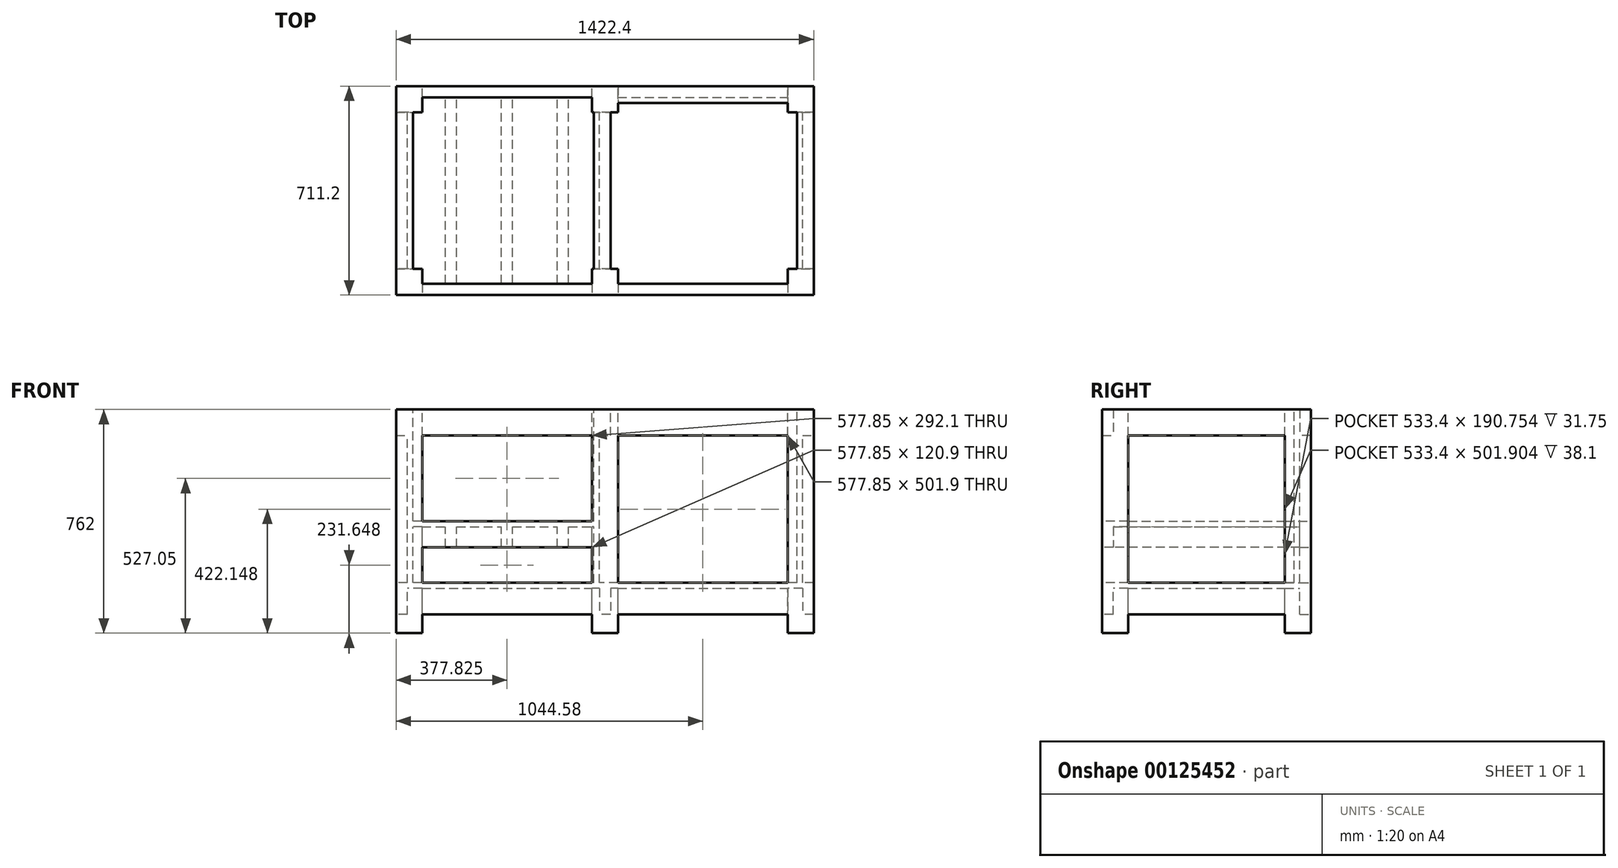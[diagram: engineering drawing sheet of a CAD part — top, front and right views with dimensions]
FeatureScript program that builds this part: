
annotation { "Feature Type Name" : "Feature", "Feature Type Description" : "" }
export const myFeature = defineFeature(function(context is Context, id is Id, definition is map)
    precondition{}
    {
        {
            var Q0;
            Q0=qCreatedBy(makeId("Top.planeOp"),FACE);
            var sketch = newSketch(context, id + "F0", { "sketchPlane" : qUnion([Q0])});
            skLineSegment(sketch, "E0", {"start": v(-711.2, 0) * mm, "end": v(711.2, 0) * mm});
            skLineSegment(sketch, "E1", {"start": v(711.2, 0) * mm, "end": v(711.2, -711.2) * mm});
            skLineSegment(sketch, "E2", {"start": v(711.2, -711.2) * mm, "end": v(-711.2, -711.2) * mm});
            skLineSegment(sketch, "E3", {"start": v(-711.2, -711.2) * mm, "end": v(-711.2, 0) * mm});
            skLineSegment(sketch, "E4.0", {"start": v(673.1, -673.1) * mm, "end": v(19.05, -673.1) * mm});
            skLineSegment(sketch, "E4.1", {"start": v(673.1, -38.1) * mm, "end": v(673.1, -673.1) * mm});
            skLineSegment(sketch, "E4.2", {"start": v(-673.1, -38.1) * mm, "end": v(-19.05, -38.1) * mm});
            skLineSegment(sketch, "E4.3", {"start": v(-673.1, -673.1) * mm, "end": v(-673.1, -38.1) * mm});
            skLineSegment(sketch, "E5", {"start": v(0, 0) * mm, "end": v(0, -711.2) * mm, "construction": true});
            skLineSegment(sketch, "E6.0", {"start": v(-19.05, -38.1) * mm, "end": v(-19.05, -673.1) * mm});
            skLineSegment(sketch, "E7.0", {"start": v(19.05, -38.1) * mm, "end": v(19.05, -673.1) * mm});
            skLineSegment(sketch, "E8.trimOffspring", {"start": v(-19.05, -673.1) * mm, "end": v(-673.1, -673.1) * mm});
            skLineSegment(sketch, "E9.trimOffspring", {"start": v(19.05, -38.1) * mm, "end": v(673.1, -38.1) * mm});
            skSolve(sketch);
        }
        {
            var Q0;
            Q0=makeQuery(id+"F0.imprint","IMPRINT",FACE,{"disambiguationData":[TD([[makeQuery(id+"F0.imprint","IMPRINT",EDGE,{"derivedFrom":sQuery(id+"F0.wireOp",EDGE,"E0")}),-1.0]])]});
            extrude(context, id + "F1", {"entities" : qUnion([Q0]), "oppositeDirection" : true, "depth" : 88.9 * mm});
        }
        {
            var Q0;
            Q0=qCreatedBy(makeId("Top.planeOp"),FACE);
            var sketch = newSketch(context, id + "F2", { "sketchPlane" : qUnion([Q0])});
            skLineSegment(sketch, "E10.bottom", {"start": v(-711.2, 0) * mm, "end": v(-622.3, 0) * mm});
            skLineSegment(sketch, "E10.top", {"start": v(-711.2, -88.9) * mm, "end": v(-622.3, -88.9) * mm});
            skLineSegment(sketch, "E10.left", {"start": v(-711.2, 0) * mm, "end": v(-711.2, -88.9) * mm});
            skLineSegment(sketch, "E10.right", {"start": v(-622.3, 0) * mm, "end": v(-622.3, -88.9) * mm});
            skLineSegment(sketch, "E11.bottom", {"start": v(-711.2, -711.2) * mm, "end": v(-622.3, -711.2) * mm});
            skLineSegment(sketch, "E11.top", {"start": v(-711.2, -622.3) * mm, "end": v(-622.3, -622.3) * mm});
            skLineSegment(sketch, "E11.left", {"start": v(-711.2, -711.2) * mm, "end": v(-711.2, -622.3) * mm});
            skLineSegment(sketch, "E11.right", {"start": v(-622.3, -711.2) * mm, "end": v(-622.3, -622.3) * mm});
            skLineSegment(sketch, "E12.bottom", {"start": v(-44.45, 0) * mm, "end": v(44.45, 0) * mm});
            skLineSegment(sketch, "E12.top", {"start": v(-44.45, -88.9) * mm, "end": v(44.45, -88.9) * mm});
            skLineSegment(sketch, "E12.left", {"start": v(-44.45, 0) * mm, "end": v(-44.45, -88.9) * mm});
            skLineSegment(sketch, "E12.right", {"start": v(44.45, 0) * mm, "end": v(44.45, -88.9) * mm});
            skLineSegment(sketch, "E13.bottom", {"start": v(-44.45, -711.2) * mm, "end": v(44.45, -711.2) * mm});
            skLineSegment(sketch, "E13.top", {"start": v(-44.45, -622.3) * mm, "end": v(44.45, -622.3) * mm});
            skLineSegment(sketch, "E13.left", {"start": v(-44.45, -711.2) * mm, "end": v(-44.45, -622.3) * mm});
            skLineSegment(sketch, "E13.right", {"start": v(44.45, -711.2) * mm, "end": v(44.45, -622.3) * mm});
            skLineSegment(sketch, "E14.bottom", {"start": v(622.3, -88.9) * mm, "end": v(711.2, -88.9) * mm});
            skLineSegment(sketch, "E14.top", {"start": v(622.3, 0) * mm, "end": v(711.2, 0) * mm});
            skLineSegment(sketch, "E14.left", {"start": v(622.3, -88.9) * mm, "end": v(622.3, 0) * mm});
            skLineSegment(sketch, "E14.right", {"start": v(711.2, -88.9) * mm, "end": v(711.2, 0) * mm});
            skLineSegment(sketch, "E15.bottom", {"start": v(622.3, -711.2) * mm, "end": v(711.2, -711.2) * mm});
            skLineSegment(sketch, "E15.top", {"start": v(622.3, -622.3) * mm, "end": v(711.2, -622.3) * mm});
            skLineSegment(sketch, "E15.left", {"start": v(622.3, -711.2) * mm, "end": v(622.3, -622.3) * mm});
            skLineSegment(sketch, "E15.right", {"start": v(711.2, -711.2) * mm, "end": v(711.2, -622.3) * mm});
            skSolve(sketch);
        }
        {
            var Q0;
            Q0 = qSketchRegion(id + "F2", true);
            extrude(context, id + "F3", {"entities" : qUnion([Q0]), "operationType" : NewBodyOperationType.ADD, "oppositeDirection" : true, "depth" : 762 * mm});
        }
        {
            var Q0;
            Q0=qCreatedBy(makeId("Top.planeOp"),FACE);
            cPlane(context, id + "F4", {"entities" : qUnion([Q0]), "cplaneType" : CPlaneType.OFFSET, "offset" : 609.6 * mm, "oppositeDirection" : true, "width" : 152.4 * mm, "height" : 152.4 * mm});
        }
        {
            var Q0;
            Q0=qCreatedBy(id+"F4.planeOp",FACE);
            var sketch = newSketch(context, id + "F5", { "sketchPlane" : qUnion([Q0])});
            skLineSegment(sketch, "E16", {"start": v(-711.2, 0) * mm, "end": v(711.2, 0) * mm});
            skLineSegment(sketch, "E17", {"start": v(711.2, 0) * mm, "end": v(711.2, -711.2) * mm});
            skLineSegment(sketch, "E18", {"start": v(711.2, -711.2) * mm, "end": v(-711.2, -711.2) * mm});
            skLineSegment(sketch, "E19", {"start": v(-711.2, -711.2) * mm, "end": v(-711.2, 0) * mm});
            skLineSegment(sketch, "E20.0", {"start": v(673.1, -673.1) * mm, "end": v(19.05, -673.1) * mm});
            skLineSegment(sketch, "E20.1", {"start": v(673.1, -38.1) * mm, "end": v(673.1, -673.1) * mm});
            skLineSegment(sketch, "E20.2", {"start": v(-673.1, -38.1) * mm, "end": v(-19.05, -38.1) * mm});
            skLineSegment(sketch, "E20.3", {"start": v(-673.1, -673.1) * mm, "end": v(-673.1, -38.1) * mm});
            skLineSegment(sketch, "E21", {"start": v(0, 1297.1) * mm, "end": v(0, -711.2) * mm, "construction": true});
            skLineSegment(sketch, "E22.0", {"start": v(-19.05, -38.1) * mm, "end": v(-19.05, -673.1) * mm});
            skLineSegment(sketch, "E23.0", {"start": v(19.05, -38.1) * mm, "end": v(19.05, -673.1) * mm});
            skLineSegment(sketch, "E24.trimOffspring", {"start": v(-19.05, -673.1) * mm, "end": v(-673.1, -673.1) * mm});
            skLineSegment(sketch, "E25.trimOffspring", {"start": v(19.05, -38.1) * mm, "end": v(673.1, -38.1) * mm});
            skSolve(sketch);
        }
        {
            var Q0;
            Q0 = qSketchRegion(id + "F5", true);
            extrude(context, id + "F6", {"entities" : qUnion([Q0]), "operationType" : NewBodyOperationType.ADD, "oppositeDirection" : true, "depth" : 88.9 * mm});
        }
        {
            var Q0;
            Q0=qCreatedBy(id+"F4.planeOp",FACE);
            var sketch = newSketch(context, id + "F7", { "sketchPlane" : qUnion([Q0])});
            skLineSegment(sketch, "E26.bottom", {"start": v(-711.2, 0) * mm, "end": v(711.2, 0) * mm});
            skLineSegment(sketch, "E26.top", {"start": v(-711.2, -711.2) * mm, "end": v(711.2, -711.2) * mm});
            skLineSegment(sketch, "E26.left", {"start": v(-711.2, 0) * mm, "end": v(-711.2, -711.2) * mm});
            skLineSegment(sketch, "E26.right", {"start": v(711.2, 0) * mm, "end": v(711.2, -711.2) * mm});
            skSolve(sketch);
        }
        {
            var Q0;
            Q0 = qSketchRegion(id + "F7", true);
            extrude(context, id + "F8", {"entities" : qUnion([Q0]), "operationType" : NewBodyOperationType.ADD, "depth" : 18.8 * mm, "hasSecondDirection" : true, "secondDirectionOppositeDirection" : true, "secondDirectionDepth" : 0.25 * mm});
        }
        {
            var Q0;
            Q0=qCreatedBy(makeId("Top.planeOp"),FACE);
            var sketch = newSketch(context, id + "F9", { "sketchPlane" : qUnion([Q0])});
            skLineSegment(sketch, "E27.bottom", {"start": v(673.1, -88.9) * mm, "end": v(654.05, -88.9) * mm});
            skLineSegment(sketch, "E27.top", {"start": v(673.1, -622.3) * mm, "end": v(654.05, -622.3) * mm});
            skLineSegment(sketch, "E27.left", {"start": v(673.1, -88.9) * mm, "end": v(673.1, -622.3) * mm});
            skLineSegment(sketch, "E27.right", {"start": v(654.05, -88.9) * mm, "end": v(654.05, -622.3) * mm});
            skLineSegment(sketch, "E28.bottom", {"start": v(622.3, -57.15) * mm, "end": v(44.45, -57.15) * mm});
            skLineSegment(sketch, "E28.top", {"start": v(622.3, -38.1) * mm, "end": v(44.45, -38.1) * mm});
            skLineSegment(sketch, "E28.left", {"start": v(622.3, -57.15) * mm, "end": v(622.3, -38.1) * mm});
            skLineSegment(sketch, "E28.right", {"start": v(44.45, -57.15) * mm, "end": v(44.45, -38.1) * mm});
            skLineSegment(sketch, "E29.bottom", {"start": v(-19.05, -88.9) * mm, "end": v(-38.1, -88.9) * mm});
            skLineSegment(sketch, "E29.top", {"start": v(-19.05, -622.3) * mm, "end": v(-38.1, -622.3) * mm});
            skLineSegment(sketch, "E29.left", {"start": v(-19.05, -88.9) * mm, "end": v(-19.05, -622.3) * mm});
            skLineSegment(sketch, "E29.right", {"start": v(-38.1, -88.9) * mm, "end": v(-38.1, -622.3) * mm});
            skLineSegment(sketch, "E30.bottom", {"start": v(-654.05, -88.9) * mm, "end": v(-673.1, -88.9) * mm});
            skLineSegment(sketch, "E30.top", {"start": v(-654.05, -622.3) * mm, "end": v(-673.1, -622.3) * mm});
            skLineSegment(sketch, "E30.left", {"start": v(-654.05, -88.9) * mm, "end": v(-654.05, -622.3) * mm});
            skLineSegment(sketch, "E30.right", {"start": v(-673.1, -88.9) * mm, "end": v(-673.1, -622.3) * mm});
            skSolve(sketch);
        }
        {
            var Q0;
            Q0 = qSketchRegion(id + "F9", true);
            extrude(context, id + "F10", {"entities" : qUnion([Q0]), "operationType" : NewBodyOperationType.ADD, "endBound" : BoundingType.UP_TO_NEXT, "oppositeDirection" : true, "depth" : 25.4 * mm});
        }
        {
            var Q0;
            Q0=qCreatedBy(makeId("Top.planeOp"),FACE);
            cPlane(context, id + "F11", {"entities" : qUnion([Q0]), "cplaneType" : CPlaneType.OFFSET, "offset" : 381 * mm, "oppositeDirection" : true, "width" : 152.4 * mm, "height" : 152.4 * mm});
        }
        {
            var Q0;
            Q0=qCreatedBy(id+"F11.planeOp",FACE);
            var sketch = newSketch(context, id + "F12", { "sketchPlane" : qUnion([Q0])});
            skLineSegment(sketch, "E31.bottom", {"start": v(-711.2, 0) * mm, "end": v(0, 0) * mm});
            skLineSegment(sketch, "E31.top", {"start": v(-711.2, -38.1) * mm, "end": v(-542.93, -38.1) * mm});
            skLineSegment(sketch, "E31.left", {"start": v(-711.2, 0) * mm, "end": v(-711.2, -38.1) * mm});
            skLineSegment(sketch, "E31.right", {"start": v(0, 0) * mm, "end": v(0, -38.1) * mm});
            skLineSegment(sketch, "E32.bottom", {"start": v(-711.2, -711.2) * mm, "end": v(0, -711.2) * mm});
            skLineSegment(sketch, "E32.top", {"start": v(-711.2, -673.1) * mm, "end": v(-542.93, -673.1) * mm});
            skLineSegment(sketch, "E32.left", {"start": v(-711.2, -711.2) * mm, "end": v(-711.2, -673.1) * mm});
            skLineSegment(sketch, "E32.right", {"start": v(0, -711.2) * mm, "end": v(0, -673.1) * mm});
            skLineSegment(sketch, "E33", {"start": v(-333.38, -38.1) * mm, "end": v(-333.38, -673.1) * mm, "construction": true});
            skLineSegment(sketch, "E34.0", {"start": v(-314.33, -38.1) * mm, "end": v(-314.33, -673.1) * mm});
            skLineSegment(sketch, "E35.0", {"start": v(-352.43, -38.1) * mm, "end": v(-352.43, -673.1) * mm});
            skLineSegment(sketch, "E36.trimOffspring", {"start": v(-314.33, -38.1) * mm, "end": v(-161.93, -38.1) * mm});
            skLineSegment(sketch, "E37.trimOffspring", {"start": v(-314.33, -673.1) * mm, "end": v(-161.93, -673.1) * mm});
            skLineSegment(sketch, "E38", {"start": v(-504.83, -38.1) * mm, "end": v(-504.83, -673.1) * mm});
            skLineSegment(sketch, "E39", {"start": v(-161.93, -38.1) * mm, "end": v(-161.93, -673.1) * mm});
            skLineSegment(sketch, "E40.0", {"start": v(-542.93, -38.1) * mm, "end": v(-542.93, -673.1) * mm});
            skLineSegment(sketch, "E41.0", {"start": v(-123.83, -38.1) * mm, "end": v(-123.83, -673.1) * mm});
            skLineSegment(sketch, "E42.trimOffspring", {"start": v(-504.83, -673.1) * mm, "end": v(-352.43, -673.1) * mm});
            skLineSegment(sketch, "E43.trimOffspring", {"start": v(-123.83, -673.1) * mm, "end": v(0, -673.1) * mm});
            skLineSegment(sketch, "E44.trimOffspring", {"start": v(-504.83, -38.1) * mm, "end": v(-352.43, -38.1) * mm});
            skLineSegment(sketch, "E45.trimOffspring", {"start": v(-123.83, -38.1) * mm, "end": v(0, -38.1) * mm});
            skLineSegment(sketch, "E46", {"start": v(-44.45, -38.1) * mm, "end": v(-622.3, -38.1) * mm, "construction": true});
            skSolve(sketch);
        }
        {
            var Q0;
            Q0 = qSketchRegion(id + "F12", true);
            extrude(context, id + "F13", {"entities" : qUnion([Q0]), "operationType" : NewBodyOperationType.ADD, "oppositeDirection" : true, "depth" : 88.9 * mm});
        }
        {
            var Q0;
            Q0=makeQuery(id+"F13.opExtrude","CAP_FACE",FACE,{"disambiguationData":[OSD([sQuery(id+"F12.wireOp",EDGE,"E31.bottom"),sQuery(id+"F12.wireOp",EDGE,"E31.top"),sQuery(id+"F12.wireOp",EDGE,"E31.left"),sQuery(id+"F12.wireOp",EDGE,"E31.right"),sQuery(id+"F12.wireOp",EDGE,"E32.bottom"),sQuery(id+"F12.wireOp",EDGE,"E32.top"),sQuery(id+"F12.wireOp",EDGE,"E32.left"),sQuery(id+"F12.wireOp",EDGE,"E32.right"),sQuery(id+"F12.wireOp",EDGE,"E34.0"),sQuery(id+"F12.wireOp",EDGE,"E35.0"),sQuery(id+"F12.wireOp",EDGE,"E36.trimOffspring"),sQuery(id+"F12.wireOp",EDGE,"E37.trimOffspring"),sQuery(id+"F12.wireOp",EDGE,"E38"),sQuery(id+"F12.wireOp",EDGE,"E39"),sQuery(id+"F12.wireOp",EDGE,"E40.0"),sQuery(id+"F12.wireOp",EDGE,"E41.0"),sQuery(id+"F12.wireOp",EDGE,"E42.trimOffspring"),sQuery(id+"F12.wireOp",EDGE,"E43.trimOffspring"),sQuery(id+"F12.wireOp",EDGE,"E44.trimOffspring"),sQuery(id+"F12.wireOp",EDGE,"E45.trimOffspring")])],"isStart":true});
            var sketch = newSketch(context, id + "F14", { "sketchPlane" : qUnion([Q0])});
            skLineSegment(sketch, "E47.bottom", {"start": v(-673.1, -38.1) * mm, "end": v(-19.05, -38.1) * mm});
            skLineSegment(sketch, "E47.top", {"start": v(-673.1, -673.1) * mm, "end": v(-19.05, -673.1) * mm});
            skLineSegment(sketch, "E47.left", {"start": v(-673.1, -38.1) * mm, "end": v(-673.1, -673.1) * mm});
            skLineSegment(sketch, "E47.right", {"start": v(-19.05, -38.1) * mm, "end": v(-19.05, -673.1) * mm});
            skSolve(sketch);
        }
        {
            var Q0;
            Q0 = qSketchRegion(id + "F14", true);
            extrude(context, id + "F15", {"entities" : qUnion([Q0]), "operationType" : NewBodyOperationType.ADD, "oppositeDirection" : true, "depth" : 19.05 * mm});
        }
    });
